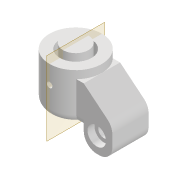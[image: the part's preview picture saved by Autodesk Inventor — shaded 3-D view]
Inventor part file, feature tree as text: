
AUTODESK INVENTOR PART (.ipt)
format: ipt  version: 2022 (Build 260153000, 153)  size: 214,528 bytes
history: native  units: mm
features: extrude x7, sketch x7, projected_geometry x4, fillet x2, plane x1, mirror x1
ambient origin geometry x8: Origin, YZ Plane, XZ Plane, XY Plane, X Axis, Y Axis, Z Axis, Center Point
bodies: Solid1 (feature_tree)
feature tree (22):
  extrude  "Extrusion1"  Depth=12.2mm
  extrude  "Extrusion2"  Depth=15.0mm TaperAngle=0.0deg
  extrude  "Extrusion3"  Depth=3.0mm TaperAngle=0.0deg
  plane  "Work Plane1"
  sketch  "Sketch5"  dims[d11=5.0mm d12=6.0mm d13=6.0mm d14=15.0mm]
  extrude  "Extrusion4"  Depth=7.1mm
  mirror  "Mirror2"
  extrude  "Extrusion5"  Depth=6.0mm
  fillet  "Fillet3"  Radius=6.0mm
  fillet  "Fillet5"  Radius=15.0mm
  extrude  "Extrusion9"  Depth=7.0mm TaperAngle=0.0deg
  extrude  "Extrusion10"  Depth=8.0mm
  sketch  "Sketch1"  dims[d0=9.8mm d1=12.2mm]
  sketch  "Sketch2"  dims[d2=4.0mm d3=15.0mm d4=0.0mm]
  projected_geometry  "Projected Loop1"
  sketch  "Sketch3"  dims[d5=2.0mm d6=0.0mm d7=3.0mm d8=0.0mm]
  projected_geometry  "Projected Loop2"
  sketch  "Sketch4"  dims[d9=0.0mm d10=7.1mm]
  projected_geometry  "Projected Loop3"
  sketch  "Sketch9"  dims[d15=6.0mm d16=7.0mm d17=0.0mm]
  sketch  "Sketch10"  dims[d20=100.0mm d21=0.0mm d22=5.0mm d24=3.0mm d34=4.2mm d35=8.6mm d36=0.0mm d37=2.1mm d38=8.0mm d39=100.0mm d40=0.0mm]
  projected_geometry  "Projected Loop8"
